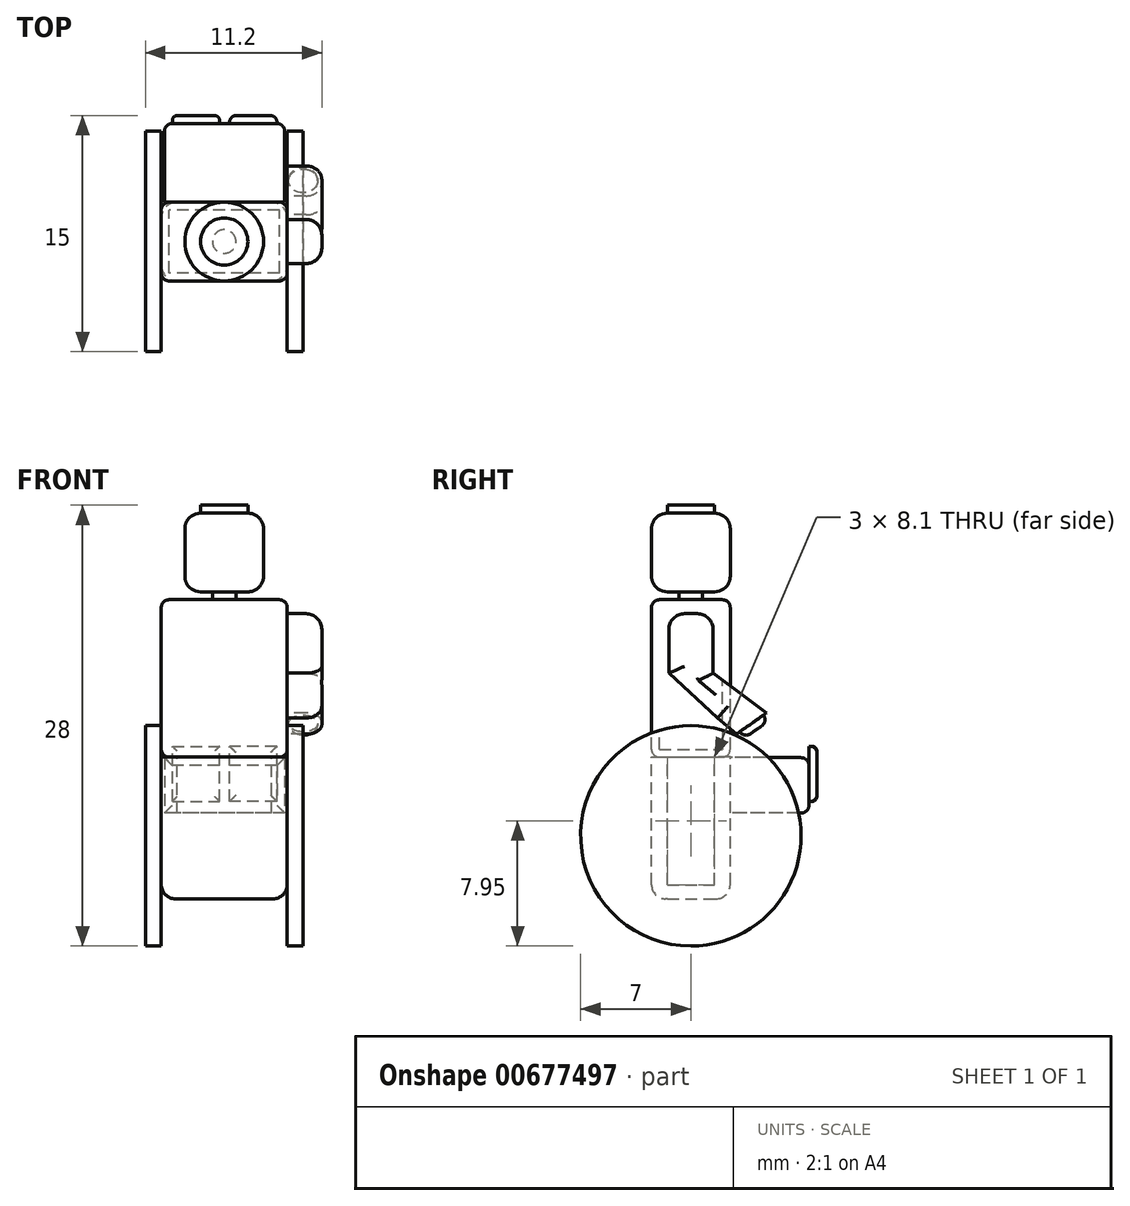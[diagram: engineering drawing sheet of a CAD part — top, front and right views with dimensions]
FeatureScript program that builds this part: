
annotation { "Feature Type Name" : "Feature", "Feature Type Description" : "" }
export const myFeature = defineFeature(function(context is Context, id is Id, definition is map)
    precondition{}
    {
        {
            var Q0;
            Q0=qCreatedBy(makeId("Top.planeOp"),FACE);
            var sketch = newSketch(context, id + "F0", { "sketchPlane" : qUnion([Q0])});
            skCircle(sketch, "E0", {"center": v(0, 0) * mm, "radius": 0.75 * mm});
            skSolve(sketch);
        }
        {
            var Q0;
            Q0 = qSketchRegion(id + "F0", true);
            extrude(context, id + "F1", {"entities" : qUnion([Q0]), "depth" : 0.5 * mm, "offsetDistance" : 25 * mm});
        }
        {
            var Q0;
            Q0=makeQuery(id+"F1.opExtrude","CAP_FACE",FACE,{"disambiguationData":[OSD([sQuery(id+"F0.wireOp",EDGE,"E0")])],"isStart":false});
            var sketch = newSketch(context, id + "F2", { "sketchPlane" : qUnion([Q0])});
            skCircle(sketch, "E1", {"center": v(0, 0) * mm, "radius": 2.5 * mm});
            skSolve(sketch);
        }
        {
            var Q0;
            Q0 = qSketchRegion(id + "F2", true);
            extrude(context, id + "F3", {"entities" : qUnion([Q0]), "operationType" : NewBodyOperationType.ADD, "depth" : 5 * mm, "offsetDistance" : 25 * mm});
        }
        {
            var Q0;
            Q0=makeQuery(id+"F3.opExtrude","CAP_EDGE",EDGE,{"disambiguationData":[OSD([sQuery(id+"F2.wireOp",EDGE,"E1")])],"isStart":true});
            fillet(context, id + "F4", {"entities" : qUnion([Q0]), "radius" : 1 * mm, "tangentPropagation" : true, "allowEdgeOverflow" : false});
        }
        {
            var Q0;
            Q0=makeQuery(id+"F3.opExtrude","CAP_EDGE",EDGE,{"disambiguationData":[OSD([sQuery(id+"F2.wireOp",EDGE,"E1")])],"isStart":false});
            var Q1;
            Q1=makeQuery(id+"F3.opExtrude","SWEPT_FACE",FACE,{"disambiguationData":[OSD([sQuery(id+"F2.wireOp",EDGE,"E1")])]});
            fillet(context, id + "F5", {"entities" : qUnion([Q0, Q1]), "radius" : 1 * mm, "tangentPropagation" : true, "allowEdgeOverflow" : false});
        }
        {
            var Q0;
            Q0=makeQuery(id+"F3.opExtrude","CAP_FACE",FACE,{"disambiguationData":[OSD([sQuery(id+"F2.wireOp",EDGE,"E1")])],"isStart":false});
            var sketch = newSketch(context, id + "F6", { "sketchPlane" : qUnion([Q0])});
            skCircle(sketch, "E2", {"center": v(0, 0) * mm, "radius": 1.5 * mm});
            skSolve(sketch);
        }
        {
            var Q0;
            Q0 = qSketchRegion(id + "F6", true);
            extrude(context, id + "F7", {"entities" : qUnion([Q0]), "operationType" : NewBodyOperationType.ADD, "depth" : 0.5 * mm, "offsetDistance" : 25 * mm});
        }
        {
            var Q0;
            Q0=makeQuery(id+"F1.opExtrude","CAP_FACE",FACE,{"disambiguationData":[OSD([sQuery(id+"F0.wireOp",EDGE,"E0")])],"isStart":true});
            var sketch = newSketch(context, id + "F8", { "sketchPlane" : qUnion([Q0])});
            skLineSegment(sketch, "E3.bottom", {"start": v(4, 2.5) * mm, "end": v(-4, 2.5) * mm});
            skLineSegment(sketch, "E3.top", {"start": v(4, -2.5) * mm, "end": v(-4, -2.5) * mm});
            skLineSegment(sketch, "E3.left", {"start": v(4, 2.5) * mm, "end": v(4, -2.5) * mm});
            skLineSegment(sketch, "E3.right", {"start": v(-4, 2.5) * mm, "end": v(-4, -2.5) * mm});
            skPoint(sketch, "E3.middle", {"position": v(0, 0) * mm});
            skSolve(sketch);
        }
        {
            var Q0;
            Q0=makeQuery(id+"F8.imprint","IMPRINT",FACE,{"disambiguationData":[TD([[makeQuery(id+"F8.imprint","IMPRINT",EDGE,{"derivedFrom":sQuery(id+"F8.wireOp",EDGE,"E3.bottom")}),1.0]])]});
            var Q1;
            Q1=makeQuery(id+"F8.imprint","IMPRINT",FACE,{"disambiguationData":[TD([[makeQuery(id+"F8.imprint","IMPRINT",EDGE,{"derivedFrom":makeQuery(id+"F1.opExtrude","CAP_EDGE",EDGE,{"disambiguationData":[OSD([sQuery(id+"F0.wireOp",EDGE,"E0")])],"isStart":true})}),-1.0]])]});
            extrude(context, id + "F9", {"entities" : qUnion([Q0, Q1]), "operationType" : NewBodyOperationType.ADD, "depth" : 10 * mm, "offsetDistance" : 25 * mm});
        }
        {
            var Q0;
            Q0=makeQuery(id+"F9.opExtrude","CAP_EDGE",EDGE,{"disambiguationData":[OSD([sQuery(id+"F8.wireOp",EDGE,"E3.top")])],"isStart":true});
            var Q1;
            Q1=makeQuery(id+"F9.opExtrude","CAP_EDGE",EDGE,{"disambiguationData":[OSD([sQuery(id+"F8.wireOp",EDGE,"E3.bottom")])],"isStart":true});
            var Q2;
            Q2=makeQuery(id+"F9.opExtrude","CAP_EDGE",EDGE,{"disambiguationData":[OSD([sQuery(id+"F8.wireOp",EDGE,"E3.left")])],"isStart":true});
            var Q3;
            Q3=makeQuery(id+"F9.opExtrude","CAP_EDGE",EDGE,{"disambiguationData":[OSD([sQuery(id+"F8.wireOp",EDGE,"E3.right")])],"isStart":true});
            fillet(context, id + "F10", {"entities" : qUnion([Q0, Q1, Q2, Q3]), "radius" : 0.5 * mm, "tangentPropagation" : true, "allowEdgeOverflow" : false});
        }
        {
            var Q0;
            Q0=makeQuery(id+"F9.opExtrude","SWEPT_EDGE",EDGE,{"disambiguationData":[OSD([sQuery(id+"F8.wireOp",EDGE,"E3.top"),sQuery(id+"F8.wireOp",EDGE,"E3.right")])]});
            var Q1;
            Q1=makeQuery(id+"F9.opExtrude","SWEPT_EDGE",EDGE,{"disambiguationData":[OSD([sQuery(id+"F8.wireOp",EDGE,"E3.bottom"),sQuery(id+"F8.wireOp",EDGE,"E3.right")])]});
            var Q2;
            Q2=makeQuery(id+"F9.opExtrude","SWEPT_EDGE",EDGE,{"disambiguationData":[OSD([sQuery(id+"F8.wireOp",EDGE,"E3.top"),sQuery(id+"F8.wireOp",EDGE,"E3.left")])]});
            var Q3;
            Q3=makeQuery(id+"F9.opExtrude","SWEPT_EDGE",EDGE,{"disambiguationData":[OSD([sQuery(id+"F8.wireOp",EDGE,"E3.bottom"),sQuery(id+"F8.wireOp",EDGE,"E3.left")])]});
            var Q4;
            Q4=makeQuery(id+"F9.opExtrude","CAP_EDGE",EDGE,{"disambiguationData":[OSD([sQuery(id+"F8.wireOp",EDGE,"E3.bottom")])],"isStart":false});
            var Q5;
            Q5=makeQuery(id+"F9.opExtrude","CAP_EDGE",EDGE,{"disambiguationData":[OSD([sQuery(id+"F8.wireOp",EDGE,"E3.right")])],"isStart":false});
            var Q6;
            Q6=makeQuery(id+"F9.opExtrude","CAP_EDGE",EDGE,{"disambiguationData":[OSD([sQuery(id+"F8.wireOp",EDGE,"E3.top")])],"isStart":false});
            var Q7;
            Q7=makeQuery(id+"F9.opExtrude","CAP_EDGE",EDGE,{"disambiguationData":[OSD([sQuery(id+"F8.wireOp",EDGE,"E3.left")])],"isStart":false});
            fillet(context, id + "F11", {"entities" : qUnion([Q0, Q1, Q2, Q3, Q4, Q5, Q6, Q7]), "radius" : 0.5 * mm, "tangentPropagation" : true, "allowEdgeOverflow" : false});
        }
        {
            var Q0;
            Q0=makeQuery(id+"F9.opExtrude","SWEPT_FACE",FACE,{"disambiguationData":[OSD([sQuery(id+"F8.wireOp",EDGE,"E3.left")])]});
            var sketch = newSketch(context, id + "F12", { "sketchPlane" : qUnion([Q0])});
            skLineSegment(sketch, "E4.top", {"start": v(-1.4, -0.89) * mm, "end": v(1.4, -0.89) * mm});
            skLineSegment(sketch, "E4.left", {"start": v(-1.4, -2.57) * mm, "end": v(-1.4, -0.89) * mm});
            skLineSegment(sketch, "E4.right", {"start": v(1.4, -2.57) * mm, "end": v(1.4, -0.89) * mm});
            skLineSegment(sketch, "E5.left", {"start": v(-1.4, -2.57) * mm, "end": v(-1.4, -4.67) * mm});
            skLineSegment(sketch, "E5.right", {"start": v(1.4, -2.57) * mm, "end": v(1.4, -4.67) * mm});
            skLineSegment(sketch, "E6", {"start": v(1.4, -4.67) * mm, "end": v(3.53, -6.25) * mm});
            skLineSegment(sketch, "E7", {"start": v(3.53, -6.25) * mm, "end": v(4.8, -7.2) * mm});
            skPoint(sketch, "E8.trimOffspring.end.orphan", {"position": v(-1.4, -6.76) * mm});
            skPoint(sketch, "E9.orphan", {"position": v(1.4, -6.76) * mm});
            skLineSegment(sketch, "E10", {"start": v(-1.4, -4.67) * mm, "end": v(1.7, -7.5) * mm});
            skLineSegment(sketch, "E11", {"start": v(1.7, -7.5) * mm, "end": v(2.9, -8.54) * mm});
            skLineSegment(sketch, "E12", {"start": v(2.9, -8.54) * mm, "end": v(4.8, -7.2) * mm});
            skPoint(sketch, "E13.end.orphan", {"position": v(3.53, -8.08) * mm});
            skSolve(sketch);
        }
        {
            var Q0;
            Q0 = qSketchRegion(id + "F12", true);
            extrude(context, id + "F13", {"entities" : qUnion([Q0]), "operationType" : NewBodyOperationType.ADD, "depth" : 2.2 * mm, "offsetDistance" : 25 * mm});
        }
        {
            var Q0;
            Q0=makeQuery(id+"F13.opExtrude","SWEPT_EDGE",EDGE,{"disambiguationData":[OSD([sQuery(id+"F12.wireOp",EDGE,"E4.top"),sQuery(id+"F12.wireOp",EDGE,"E4.left")])]});
            var Q1;
            Q1=makeQuery(id+"F13.opExtrude","SWEPT_EDGE",EDGE,{"disambiguationData":[OSD([sQuery(id+"F12.wireOp",EDGE,"E4.top"),sQuery(id+"F12.wireOp",EDGE,"E4.right")])]});
            var Q2;
            Q2=makeQuery(id+"F13.opExtrude","CAP_EDGE",EDGE,{"disambiguationData":[OSD([sQuery(id+"F12.wireOp",EDGE,"E6")])],"isStart":false});
            var Q3;
            Q3=makeQuery(id+"F13.opExtrude","CAP_EDGE",EDGE,{"disambiguationData":[OSD([sQuery(id+"F12.wireOp",EDGE,"E4.right"),sQuery(id+"F12.wireOp",EDGE,"E5.right")])],"isStart":false});
            var Q4;
            Q4=makeQuery(id+"F13.opExtrude","CAP_EDGE",EDGE,{"disambiguationData":[OSD([sQuery(id+"F12.wireOp",EDGE,"E4.left"),sQuery(id+"F12.wireOp",EDGE,"E5.left")])],"isStart":false});
            var Q5;
            Q5=makeQuery(id+"F13.opExtrude","CAP_EDGE",EDGE,{"disambiguationData":[OSD([sQuery(id+"F12.wireOp",EDGE,"E10")])],"isStart":false});
            var Q6;
            Q6=makeQuery(id+"F13.opExtrude","CAP_EDGE",EDGE,{"disambiguationData":[OSD([sQuery(id+"F12.wireOp",EDGE,"E11")])],"isStart":false});
            var Q7;
            Q7=makeQuery(id+"F13.opExtrude","CAP_EDGE",EDGE,{"disambiguationData":[OSD([sQuery(id+"F12.wireOp",EDGE,"E7")])],"isStart":false});
            fillet(context, id + "F14", {"entities" : qUnion([Q0, Q1, Q2, Q3, Q4, Q5, Q6, Q7]), "radius" : 1 * mm, "tangentPropagation" : true, "allowEdgeOverflow" : false});
        }
        {
            var Q0;
            Q0=makeQuery(id+"F13.opExtrude","CAP_EDGE",EDGE,{"disambiguationData":[OSD([sQuery(id+"F12.wireOp",EDGE,"E4.top")])],"isStart":false});
            fillet(context, id + "F15", {"entities" : qUnion([Q0]), "radius" : 1 * mm, "tangentPropagation" : true, "allowEdgeOverflow" : false});
        }
        {
            var Q0;
            Q0=makeQuery(id+"F9.opExtrude","CAP_FACE",FACE,{"disambiguationData":[OSD([sQuery(id+"F8.wireOp",EDGE,"E3.bottom"),sQuery(id+"F8.wireOp",EDGE,"E3.top"),sQuery(id+"F8.wireOp",EDGE,"E3.left"),sQuery(id+"F8.wireOp",EDGE,"E3.right")])],"isStart":false});
            var sketch = newSketch(context, id + "F16", { "sketchPlane" : qUnion([Q0])});
            skLineSegment(sketch, "E14.bottom", {"start": v(-4, 2.5) * mm, "end": v(4, 2.5) * mm});
            skLineSegment(sketch, "E14.top", {"start": v(-4, -2.5) * mm, "end": v(4, -2.5) * mm});
            skLineSegment(sketch, "E14.left", {"start": v(-4, 2.5) * mm, "end": v(-4, -2.5) * mm});
            skLineSegment(sketch, "E14.right", {"start": v(4, 2.5) * mm, "end": v(4, -2.5) * mm});
            skPoint(sketch, "E14.middle", {"position": v(0, 0) * mm});
            skSolve(sketch);
        }
        {
            var Q0;
            Q0 = qSketchRegion(id + "F16", true);
            extrude(context, id + "F17", {"entities" : qUnion([Q0]), "operationType" : NewBodyOperationType.ADD, "depth" : 9 * mm, "offsetDistance" : 25 * mm});
        }
        {
            var Q0;
            Q0=makeQuery(id+"F17.opExtrude","SWEPT_EDGE",EDGE,{"disambiguationData":[OSD([sQuery(id+"F16.wireOp",EDGE,"E14.top"),sQuery(id+"F16.wireOp",EDGE,"E14.right")])]});
            var Q1;
            Q1=makeQuery(id+"F17.opExtrude","SWEPT_EDGE",EDGE,{"disambiguationData":[OSD([sQuery(id+"F16.wireOp",EDGE,"E14.bottom"),sQuery(id+"F16.wireOp",EDGE,"E14.right")])]});
            var Q2;
            Q2=makeQuery(id+"F17.opExtrude","SWEPT_EDGE",EDGE,{"disambiguationData":[OSD([sQuery(id+"F16.wireOp",EDGE,"E14.top"),sQuery(id+"F16.wireOp",EDGE,"E14.left")])]});
            var Q3;
            Q3=makeQuery(id+"F17.opExtrude","SWEPT_EDGE",EDGE,{"disambiguationData":[OSD([sQuery(id+"F16.wireOp",EDGE,"E14.bottom"),sQuery(id+"F16.wireOp",EDGE,"E14.left")])]});
            fillet(context, id + "F18", {"entities" : qUnion([Q0, Q1, Q2, Q3]), "radius" : 1 * mm, "tangentPropagation" : true, "allowEdgeOverflow" : false});
        }
        {
            var Q0;
            Q0=makeQuery(id+"F17.opExtrude","CAP_FACE",FACE,{"disambiguationData":[OSD([sQuery(id+"F16.wireOp",EDGE,"E14.bottom"),sQuery(id+"F16.wireOp",EDGE,"E14.top"),sQuery(id+"F16.wireOp",EDGE,"E14.left"),sQuery(id+"F16.wireOp",EDGE,"E14.right")])],"isStart":false});
            fillet(context, id + "F19", {"entities" : qUnion([Q0]), "radius" : 0.9 * mm, "tangentPropagation" : true, "allowEdgeOverflow" : false});
        }
        {
            var Q0;
            Q0=makeQuery(id+"F17.opExtrude","SWEPT_FACE",FACE,{"disambiguationData":[OSD([sQuery(id+"F16.wireOp",EDGE,"E14.right")])]});
            var sketch = newSketch(context, id + "F20", { "sketchPlane" : qUnion([Q0])});
            skCircle(sketch, "E15", {"center": v(0, -15) * mm, "radius": 7 * mm});
            skSolve(sketch);
        }
        {
            var Q0;
            Q0 = qSketchRegion(id + "F20", true);
            extrude(context, id + "F21", {"entities" : qUnion([Q0]), "operationType" : NewBodyOperationType.ADD, "depth" : 1 * mm, "offsetDistance" : 25 * mm});
        }
        {
            var Q0;
            Q0=makeQuery(id+"F17.opExtrude","SWEPT_FACE",FACE,{"disambiguationData":[OSD([sQuery(id+"F16.wireOp",EDGE,"E14.top")])]});
            var sketch = newSketch(context, id + "F22", { "sketchPlane" : qUnion([Q0])});
            skLineSegment(sketch, "E16.bottom", {"start": v(-3.85, -10.03) * mm, "end": v(3.8, -10.03) * mm});
            skLineSegment(sketch, "E16.top", {"start": v(-3.85, -13.55) * mm, "end": v(3.8, -13.55) * mm});
            skLineSegment(sketch, "E16.left", {"start": v(-3.85, -10.03) * mm, "end": v(-3.85, -13.55) * mm});
            skLineSegment(sketch, "E16.right", {"start": v(3.8, -10.03) * mm, "end": v(3.8, -13.55) * mm});
            skSolve(sketch);
        }
        {
            var Q0;
            Q0 = qSketchRegion(id + "F22", true);
            extrude(context, id + "F23", {"entities" : qUnion([Q0]), "operationType" : NewBodyOperationType.ADD, "depth" : 5 * mm, "offsetDistance" : 25 * mm});
        }
        {
            var Q0;
            Q0=makeQuery(id+"F23.opExtrude","CAP_EDGE",EDGE,{"disambiguationData":[OSD([sQuery(id+"F22.wireOp",EDGE,"E16.bottom")])],"isStart":false});
            var Q1;
            Q1=makeQuery(id+"F23.opExtrude","CAP_EDGE",EDGE,{"disambiguationData":[OSD([sQuery(id+"F22.wireOp",EDGE,"E16.top")])],"isStart":false});
            var Q2;
            Q2=makeQuery(id+"F23.opExtrude","CAP_EDGE",EDGE,{"disambiguationData":[OSD([sQuery(id+"F22.wireOp",EDGE,"E16.left")])],"isStart":false});
            var Q3;
            Q3=makeQuery(id+"F23.opExtrude","CAP_EDGE",EDGE,{"disambiguationData":[OSD([sQuery(id+"F22.wireOp",EDGE,"E16.right")])],"isStart":false});
            fillet(context, id + "F24", {"entities" : qUnion([Q0, Q1, Q2, Q3]), "radius" : 0.5 * mm, "tangentPropagation" : true, "allowEdgeOverflow" : false});
        }
        {
            var Q0;
            Q0=makeQuery(id+"F23.opExtrude","CAP_FACE",FACE,{"disambiguationData":[OSD([sQuery(id+"F22.wireOp",EDGE,"E16.bottom"),sQuery(id+"F22.wireOp",EDGE,"E16.top"),sQuery(id+"F22.wireOp",EDGE,"E16.left"),sQuery(id+"F22.wireOp",EDGE,"E16.right")])],"isStart":false});
            var sketch = newSketch(context, id + "F25", { "sketchPlane" : qUnion([Q0])});
            skLineSegment(sketch, "E17.bottom", {"start": v(-3.35, -12.8) * mm, "end": v(-0.35, -12.8) * mm});
            skLineSegment(sketch, "E17.top", {"start": v(-3.35, -9.3) * mm, "end": v(-0.35, -9.3) * mm});
            skLineSegment(sketch, "E17.left", {"start": v(-3.35, -12.8) * mm, "end": v(-3.35, -9.3) * mm});
            skLineSegment(sketch, "E17.right", {"start": v(-0.35, -12.8) * mm, "end": v(-0.35, -9.3) * mm});
            skSolve(sketch);
        }
        {
            var Q0;
            Q0 = qSketchRegion(id + "F25", true);
            extrude(context, id + "F26", {"entities" : qUnion([Q0]), "operationType" : NewBodyOperationType.ADD, "depth" : 0.5 * mm, "offsetDistance" : 25 * mm});
        }
        {
            var Q0;
            Q0=makeQuery(id+"F23.opExtrude","CAP_FACE",FACE,{"disambiguationData":[OSD([sQuery(id+"F22.wireOp",EDGE,"E16.bottom"),sQuery(id+"F22.wireOp",EDGE,"E16.top"),sQuery(id+"F22.wireOp",EDGE,"E16.left"),sQuery(id+"F22.wireOp",EDGE,"E16.right")])],"isStart":false});
            var sketch = newSketch(context, id + "F27", { "sketchPlane" : qUnion([Q0])});
            skLineSegment(sketch, "E18.bottom", {"start": v(3.3, -12.8) * mm, "end": v(0.3, -12.8) * mm});
            skLineSegment(sketch, "E18.top", {"start": v(3.3, -9.3) * mm, "end": v(0.3, -9.3) * mm});
            skLineSegment(sketch, "E18.left", {"start": v(3.3, -12.8) * mm, "end": v(3.3, -9.3) * mm});
            skLineSegment(sketch, "E18.right", {"start": v(0.3, -12.8) * mm, "end": v(0.3, -9.3) * mm});
            skSolve(sketch);
        }
        {
            var Q0;
            Q0 = qSketchRegion(id + "F27", true);
            extrude(context, id + "F28", {"entities" : qUnion([Q0]), "operationType" : NewBodyOperationType.ADD, "depth" : 0.5 * mm, "offsetDistance" : 25 * mm});
        }
        {
            var Q0;
            Q0=makeQuery(id+"F26.opExtrude","CAP_EDGE",EDGE,{"disambiguationData":[OSD([sQuery(id+"F25.wireOp",EDGE,"E17.left")])],"isStart":false});
            var Q1;
            Q1=makeQuery(id+"F26.opExtrude","CAP_EDGE",EDGE,{"disambiguationData":[OSD([sQuery(id+"F25.wireOp",EDGE,"E17.top")])],"isStart":false});
            var Q2;
            Q2=makeQuery(id+"F26.opExtrude","CAP_EDGE",EDGE,{"disambiguationData":[OSD([sQuery(id+"F25.wireOp",EDGE,"E17.right")])],"isStart":false});
            var Q3;
            Q3=makeQuery(id+"F26.opExtrude","CAP_EDGE",EDGE,{"disambiguationData":[OSD([sQuery(id+"F25.wireOp",EDGE,"E17.bottom")])],"isStart":false});
            fillet(context, id + "F29", {"entities" : qUnion([Q0, Q1, Q2, Q3]), "radius" : 0.4 * mm, "tangentPropagation" : true, "allowEdgeOverflow" : false});
        }
        {
            var Q0;
            Q0=makeQuery(id+"F28.opExtrude","CAP_EDGE",EDGE,{"disambiguationData":[OSD([sQuery(id+"F27.wireOp",EDGE,"E18.top")])],"isStart":false});
            var Q1;
            Q1=makeQuery(id+"F28.opExtrude","CAP_EDGE",EDGE,{"disambiguationData":[OSD([sQuery(id+"F27.wireOp",EDGE,"E18.bottom")])],"isStart":false});
            var Q2;
            Q2=makeQuery(id+"F28.opExtrude","CAP_EDGE",EDGE,{"disambiguationData":[OSD([sQuery(id+"F27.wireOp",EDGE,"E18.left")])],"isStart":false});
            var Q3;
            Q3=makeQuery(id+"F28.opExtrude","CAP_EDGE",EDGE,{"disambiguationData":[OSD([sQuery(id+"F27.wireOp",EDGE,"E18.right")])],"isStart":false});
            fillet(context, id + "F30", {"entities" : qUnion([Q0, Q1, Q2, Q3]), "radius" : 0.3 * mm, "tangentPropagation" : true, "allowEdgeOverflow" : false});
        }
        {
            var Q0;
            Q0=makeQuery(id+"F13.opExtrude","SWEPT_FACE",FACE,{"disambiguationData":[OSD([sQuery(id+"F12.wireOp",EDGE,"E12")])]});
            var sketch = newSketch(context, id + "F31", { "sketchPlane" : qUnion([Q0])});
            skCircle(sketch, "E19", {"center": v(5.01, 1.38) * mm, "radius": 0.92 * mm});
            skSolve(sketch);
        }
        {
            var Q0;
            Q0=makeQuery(id+"F17.opExtrude","SWEPT_FACE",FACE,{"disambiguationData":[OSD([sQuery(id+"F16.wireOp",EDGE,"E14.left")])]});
            var sketch = newSketch(context, id + "F32", { "sketchPlane" : qUnion([Q0])});
            skCircle(sketch, "E20", {"center": v(0, -15) * mm, "radius": 7 * mm});
            skSolve(sketch);
        }
        {
            var Q0;
            Q0 = qSketchRegion(id + "F32", true);
            extrude(context, id + "F33", {"entities" : qUnion([Q0]), "operationType" : NewBodyOperationType.ADD, "depth" : 1 * mm, "offsetDistance" : 25 * mm});
        }
        {
            var Q0;
            Q0 = qSketchRegion(id + "F31", true);
            extrude(context, id + "F34", {"entities" : qUnion([Q0]), "operationType" : NewBodyOperationType.ADD, "depth" : 0.5 * mm, "offsetDistance" : 25 * mm});
        }
        {
            var Q0;
            Q0=makeQuery(id+"F34.opExtrude","CAP_EDGE",EDGE,{"disambiguationData":[OSD([sQuery(id+"F31.wireOp",EDGE,"E19")])],"isStart":false});
            fillet(context, id + "F35", {"entities" : qUnion([Q0]), "radius" : 0.5 * mm, "tangentPropagation" : true, "allowEdgeOverflow" : false});
        }
    });
